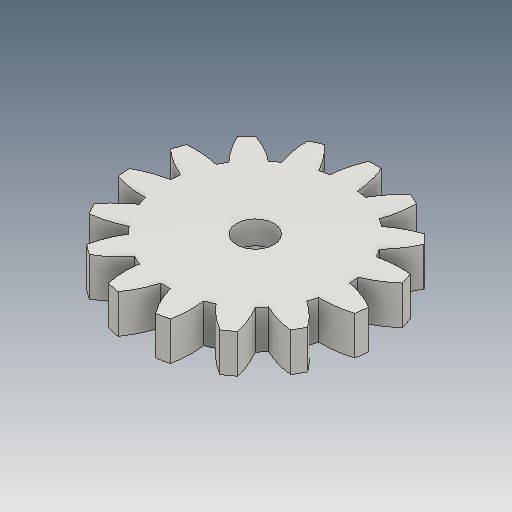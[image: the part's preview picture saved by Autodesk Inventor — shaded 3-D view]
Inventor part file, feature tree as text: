
AUTODESK INVENTOR PART (.ipt)
format: ipt  version: 2018 (Build 220112000, 112)  size: 221,184 bytes
history: native  units: mm
features: other x13, sketch x4, plane x4
ambient origin geometry x8: Origin, YZ Plane, XZ Plane, XY Plane, X Axis, Y Axis, Z Axis, Center Point
bodies: Volumenkörper1 (feature_tree)
feature tree (21):
  other  "Stirnzahnrad2"
  other  "Solid1::Stirnzahnrad2"
  other  "Bezeichnung1"
  sketch  "Sketch1"  dims[d0=10.0mm]
  sketch  "Sketch2"  dims[d16=40.0mm d17=0.0mm d41=0.0mm d43=40.0mm d46=40.0mm d47=0.0mm d48=0.0mm]
  sketch  "Skizze3"
  sketch  "Skizze4"
  plane  "XZ Plane_1"
  plane  "Work Plane2"
  plane  "Work Plane8"
  plane  "Work Plane9"
  other  "Z Axis_1"
  other  "Flä1"
  other  "Srf1::Abgeleitet"
  other  "Abstands-iMate"
  other  "Ausrichtungs-iMate"
  other  "Netz-iMate"
  other  "Achsen-iMate"
  other  "Positions-iMate"
  other  "Netz-iMate 2"
  other  "Startebenen-iMate"
